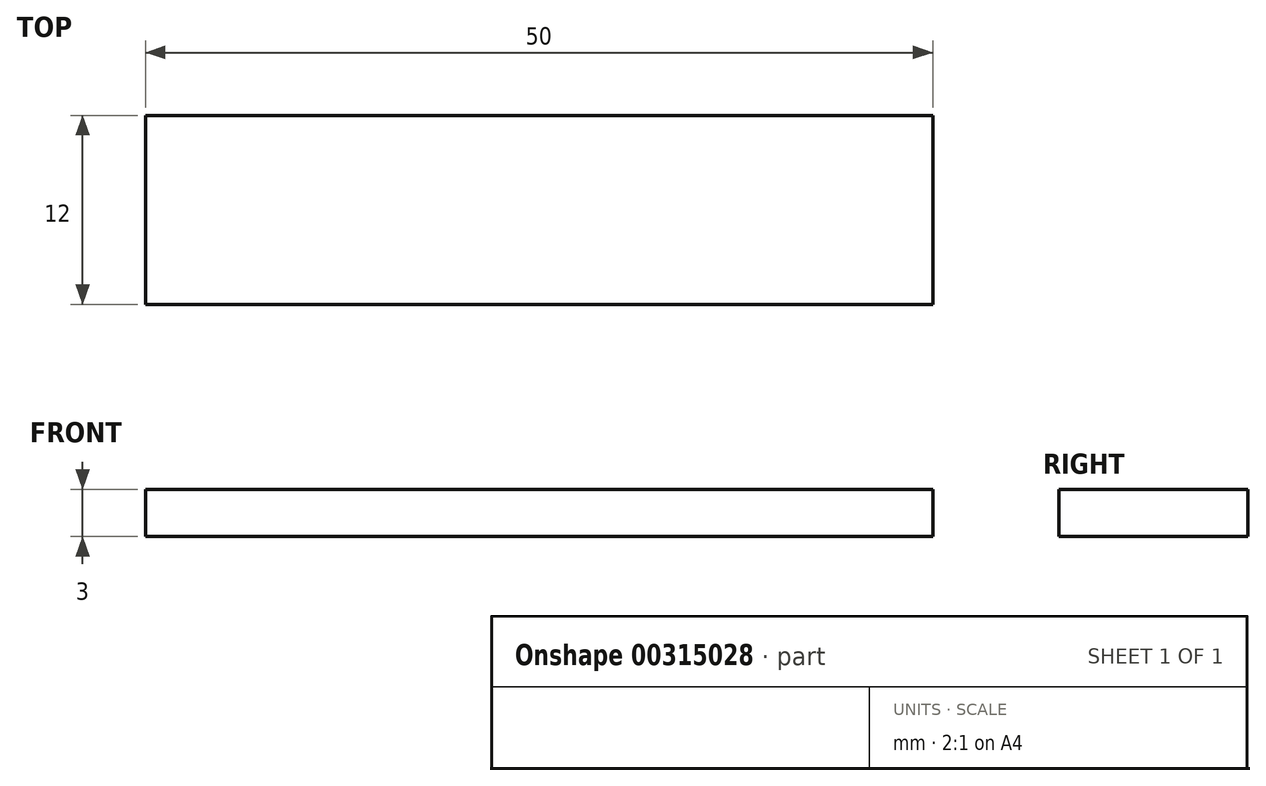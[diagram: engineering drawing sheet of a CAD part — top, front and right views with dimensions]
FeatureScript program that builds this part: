
annotation { "Feature Type Name" : "Feature", "Feature Type Description" : "" }
export const myFeature = defineFeature(function(context is Context, id is Id, definition is map)
    precondition{}
    {
        {
            var Q0;
            Q0=qCreatedBy(makeId("Top.planeOp"),FACE);
            var sketch = newSketch(context, id + "F0", { "sketchPlane" : qUnion([Q0])});
            skLineSegment(sketch, "E0.bottom", {"start": v(0, 0) * mm, "end": v(50, 0) * mm});
            skLineSegment(sketch, "E0.top", {"start": v(0, -12) * mm, "end": v(50, -12) * mm});
            skLineSegment(sketch, "E0.left", {"start": v(0, 0) * mm, "end": v(0, -12) * mm});
            skLineSegment(sketch, "E0.right", {"start": v(50, 0) * mm, "end": v(50, -12) * mm});
            skSolve(sketch);
        }
        {
            var Q0;
            Q0 = qSketchRegion(id + "F0", true);
            extrude(context, id + "F1", {"entities" : qUnion([Q0]), "depth" : 3 * mm});
        }
    });
